AUTODESK INVENTOR PART (.ipt)
format: ipt  version: 2020 (Build 240168000, 168)  size: 494,080 bytes
history: native  units: mm
features: other x4, sketch x4, extrude x2, revolve x2, pattern_circular x1
ambient origin geometry x8: Origin, YZ Plane, XZ Plane, XY Plane, X Axis, Y Axis, Z Axis, Center Point
bodies: Body1 (feature_tree)
feature tree (13):
  other  "РабПлоскость2"
  sketch  "Эскиз1"
  extrude  "Выдавливание1"  Depth=45.0mm
  revolve  "Вращение2"
  pattern_circular  "Круговой массив1"  [2 undecoded]
  other  "РабПлоскость3"
  sketch  "Эскиз3"
  other  "РабОсь3"
  revolve  "Вращение4"
  extrude  "Выдавливание3"  Depth=2.0mm
  sketch  "Эскиз5"
  sketch  "Эскиз4"
  other  "Твердое тело1"
note: 2 required parameter values undecoded (feature->parameter linkage not recoverable at this tier; creation-order binding heuristic only, values carry confidence <= 0.55)
